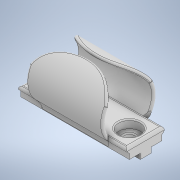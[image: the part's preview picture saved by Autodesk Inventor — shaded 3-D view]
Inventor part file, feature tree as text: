
AUTODESK INVENTOR PART (.ipt)
format: ipt  version: 2020.2 (Build 242310000, 310)  size: 445,440 bytes
history: native  units: in
note: dims shown in document units (in); Inventor stores cm internally (conversion verified against a paired STEP export)
features: sketch x6, fillet x6, extrude x4, hole x1, emboss x1
ambient origin geometry x8: Origin, YZ Plane, XZ Plane, XY Plane, X Axis, Y Axis, Z Axis, Center Point
bodies: Solid1 (feature_tree)
feature tree (18):
  extrude  "Extrusion1"  Depth=0.6in
  extrude  "Extrusion2"  Depth=0.3in
  sketch  "Sketch3"  dims[d5=0.88in d6=1.0in]
  extrude  "Extrusion3"  Depth=1.0in
  hole  "Hole1"  [1 undecoded]
  extrude  "Extrusion4"  Depth=0.3in
  fillet  "Fillet1"  Radius=0.3in
  fillet  "Fillet2"  Radius=0.1in
  fillet  "Fillet3"  Radius=2.0in
  fillet  "Fillet4"  Radius=0.2in
  fillet  "Fillet5"  Radius=0.1in
  fillet  "Fillet6"  Radius=0.5in
  emboss  "Emboss1"
  sketch  "Sketch1"  dims[d0=2.0in d1=0.6in]
  sketch  "Sketch2"  dims[d2=0.2in d3=0.0in d4=0.3in]
  sketch  "Sketch4"  dims[d7=0.06in d8=0.12in]
  sketch  "Sketch6"  dims[d9=2.0in d10=0.0in d11=0.3in d12=0.3in d13=0.1in d14=2.0in d15=0.2in d16=0.1in d17=0.0in]
  sketch  "Sketch7"  dims[d18=0.2in d19=0.75in d20=0.4in d21=0.15in d22=0.5635in d23=1.0in d24=0.8108in d35=0.5in d36=1.0in d37=0.3in d38=0.5in d39=1.0in d40=0.3in d41=0.1in d42=0.1in d43=0.06in d44=0.12in d45=1.0in d46=0.0in d47=0.125in d48=0.05in d49=0.2in d50=0.03in d51=0.02in d52=0.03in d53=0.05in d54=0.0in]
note: 1 required parameter value undecoded (feature->parameter linkage not recoverable at this tier; creation-order binding heuristic only, values carry confidence <= 0.55)
